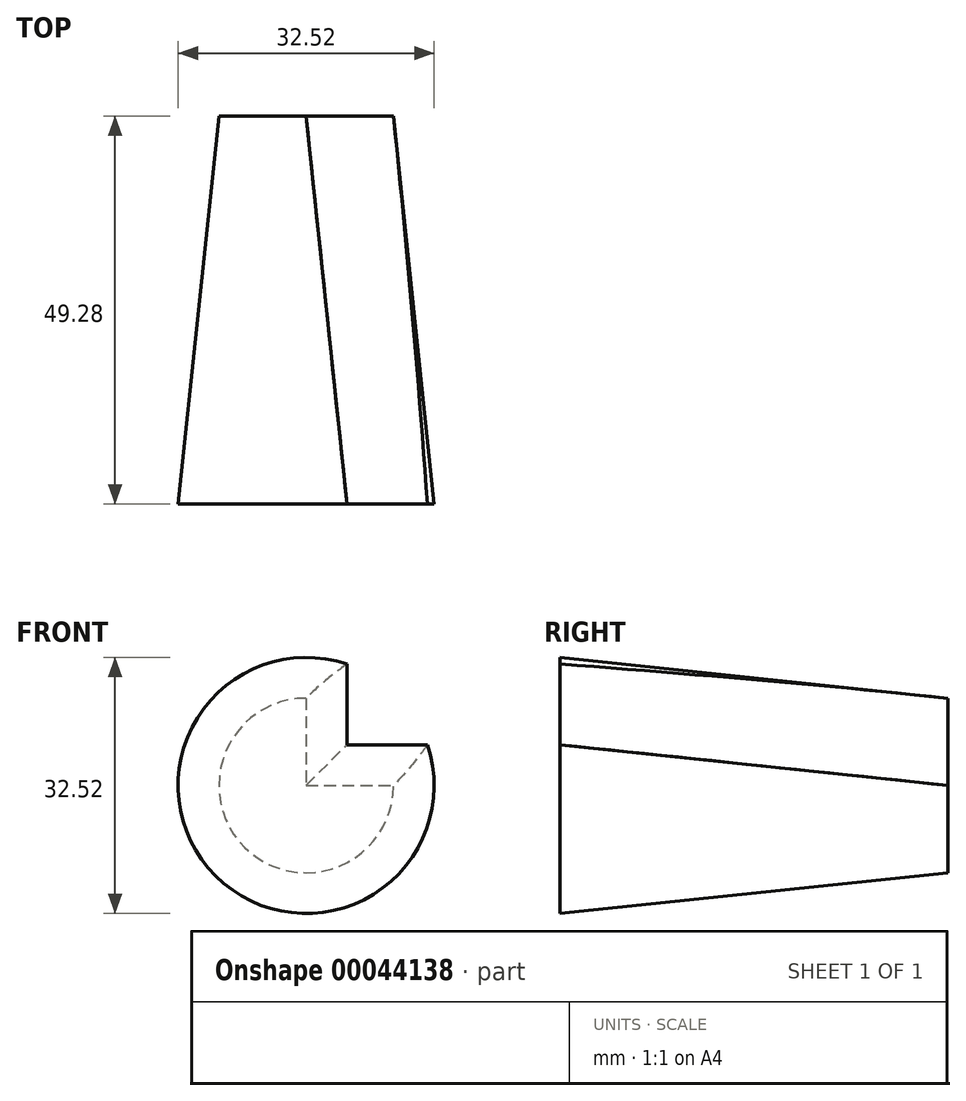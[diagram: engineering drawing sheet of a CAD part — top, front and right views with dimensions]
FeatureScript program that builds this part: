
annotation { "Feature Type Name" : "Feature", "Feature Type Description" : "" }
export const myFeature = defineFeature(function(context is Context, id is Id, definition is map)
    precondition{}
    {
        {
            var Q0;
            Q0=qCreatedBy(makeId("Front.planeOp"),FACE);
            var sketch = newSketch(context, id + "F0", { "sketchPlane" : qUnion([Q0])});
            skLineSegment(sketch, "E0", {"start": v(0, 0) * mm, "end": v(0, 114.3) * mm});
            skLineSegment(sketch, "E1", {"start": v(0, 0) * mm, "end": v(50.8, 0) * mm});
            skCircle(sketch, "E2", {"center": v(0, 114.3) * mm, "radius": 11.08 * mm});
            skCircle(sketch, "E3", {"center": v(0, 25.2) * mm, "radius": 9.32 * mm});
            skCircle(sketch, "E4", {"center": v(0, 0) * mm, "radius": 11.08 * mm});
            skCircle(sketch, "E5", {"center": v(50.8, 0) * mm, "radius": 10.12 * mm});
            skSolve(sketch);
        }
        {
            var Q0;
            {var subQ0=sQuery(id+"F0.wireOp",EDGE,"E3");var subQ1=sQuery(id+"F0.wireOp",EDGE,"E0");var subQ3=makeQuery(id+"F0.imprint","INTERSECT",VERTEX,{"disambiguationData":[OD(0.0)],"derivedFrom":[subQ1,subQ0]});Q0=makeQuery(id+"F0.imprint","IMPRINT",FACE,{"disambiguationData":[TD([[makeQuery(id+"F0.imprint","IMPRINT",EDGE,{"disambiguationData":[TD([[subQ3,-1.0]])],"derivedFrom":subQ1}),1.0]])]});}
            var Q1;
            {var subQ1=sQuery(id+"F0.wireOp",EDGE,"E1");var subQ3=sQuery(id+"F0.wireOp",EDGE,"E0");var subQ5=makeQuery(id+"F0.imprint","INTERSECT",VERTEX,{"derivedFrom":[subQ3,subQ1]});Q1=makeQuery(id+"F0.imprint","IMPRINT",FACE,{"disambiguationData":[TD([[makeQuery(id+"F0.imprint","IMPRINT",EDGE,{"disambiguationData":[TD([[subQ5,-1.0]])],"derivedFrom":subQ3}),1.0]])]});}
            extrude(context, id + "F1", {"entities" : qUnion([Q0, Q1]), "flatOperationType" : FlatOperationType.REMOVE, "offsetDistance" : 25.4 * mm, "depth" : 49.28 * mm, "hasDraft" : true, "draftAngle" : 6 * degree, "domain" : OperationDomain.MODEL});
        }
    });
